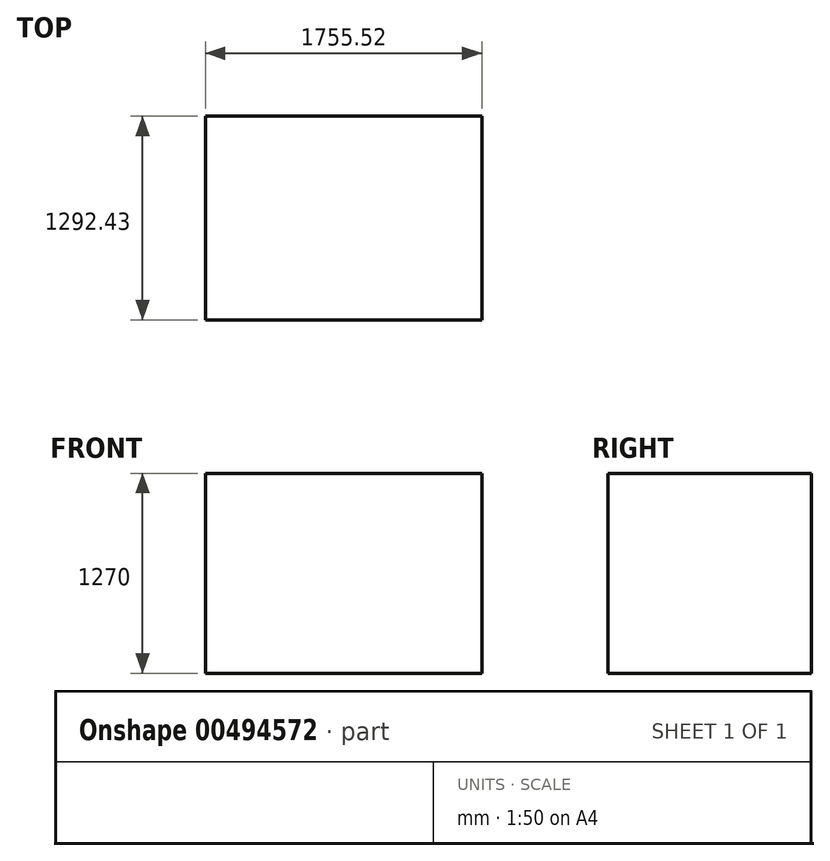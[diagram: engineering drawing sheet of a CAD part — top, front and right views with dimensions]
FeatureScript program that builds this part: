
annotation { "Feature Type Name" : "Feature", "Feature Type Description" : "" }
export const myFeature = defineFeature(function(context is Context, id is Id, definition is map)
    precondition{}
    {
        {
            var Q0;
            Q0=qCreatedBy(makeId("Top.planeOp"),FACE);
            var sketch = newSketch(context, id + "F0", { "sketchPlane" : qUnion([Q0])});
            skLineSegment(sketch, "E0.bottom", {"start": v(0, 0) * mm, "end": v(-1755.52, 0) * mm});
            skLineSegment(sketch, "E0.top", {"start": v(0, 1292.43) * mm, "end": v(-1755.52, 1292.43) * mm});
            skLineSegment(sketch, "E0.left", {"start": v(0, 0) * mm, "end": v(0, 1292.43) * mm});
            skLineSegment(sketch, "E0.right", {"start": v(-1755.52, 0) * mm, "end": v(-1755.52, 1292.43) * mm});
            skSolve(sketch);
        }
        {
            var Q0;
            Q0=makeQuery(id+"F0.imprint","IMPRINT",FACE,{"disambiguationData":[TD([[makeQuery(id+"F0.imprint","IMPRINT",EDGE,{"derivedFrom":sQuery(id+"F0.wireOp",EDGE,"E0.bottom")}),-1.0]])]});
            extrude(context, id + "F1", {"entities" : qUnion([Q0]), "depth" : 1270 * mm});
        }
    });
